# Revit family: STS-430 Контроллер_RV17_LOD400 (07.12.23)
name_source: partatom
category: Электрооборудование
revit_build: Autodesk Revit 2017 (Build: 20170118_1100(x64)
units: mm (PartAtom-declared; Revit-internal decimal feet)

## family parameters
Всегда вертикально = Нет
Конфигурация панели = Два столбца, слева направо
На основе рабочей плоскости = Да
Общий = Нет
При загрузке вырезать с полостями = Нет
Размер круглого соединителя = Использовать диаметр
Тип детали = Щит
Точка расчета площади = Нет

## types (1)
- STS-430
    ADSK_URL страницы изделия = https://stilsoft.ru
    ADSK_Единица измерения = шт.
    ADSK_Завод-изготовитель = ООО «Основа Безопасности»
    ADSK_Количество = 1
    ADSK_Марка = СТАЕ.426469.044
    ADSK_Масса = 1.3
    ADSK_Наименование = Контроллер STS-430
    ADSK_Размер_Высота = 66 мм
    ADSK_Размер_Глубина = 200 мм
    ADSK_Размер_Длина = 315 мм
    d_короба = 20 мм
    Гальваническая развязка интерфейсов RS-485 для связи контролеров = Имеется
    Грозозащита интерфейсов RS-485 для связи контролеров = Имеется
    Диапазон рабочих температур, °С = от –40 до +50
    Интеллектуальное управление питанием извещателей для компенсации пусковых токов = Имеется
    Количество входов с контролем целостности для подключения извещателей, шт. = 8
    Количество выходов для управления нагрузкой (реле), шт = 2
    Количество интерфейсов RS-232 для подключения извещателей, шт. = 1
    Количество интерфейсов RS-485 для подключения извещателей, шт. = 1
    Количество интерфейсов RS-485 для связи контролеров, шт = 2
    Максимальная дальность передачи извещений, до, км = 30 (до 75 по спец. заказу)
    Максимальная потребляемая мощность извещателей при напряжении электропитания постоянного тока 12В, Вт = 10 Вт
    Максимальная потребляемая мощность извещателей при напряжении электропитания постоянного тока 24В, Вт = 20 Вт
    Максимальная суммарная потребляемая мощность извещателей, подключенных к одному контроллеру, Вт = 20 Вт
    Максимальное количество контроллеров в одной сети, шт = 64
    Максимальное количество подключаемых извещателей в одной системе, шт = 640
    Максимальное расстояние между соседними контроллерами, км = 1 мм
    Максимальный потребляемый ток контроллера (без извещателей), А = 0 А
    Мощность = 2
    Напряжение = 12
    Напряжение переменного тока линии питания контроллеров, В = 85-265
    Напряжение постоянного тока автономного питания контроллера, В = 12
    Напряжение электропитания постоянного тока датчиков, В = 12 и 24
    Определение обрыва и короткого замыкания линий входов извещателей = Имеется
    Отметка по умолчанию = 1219 мм
